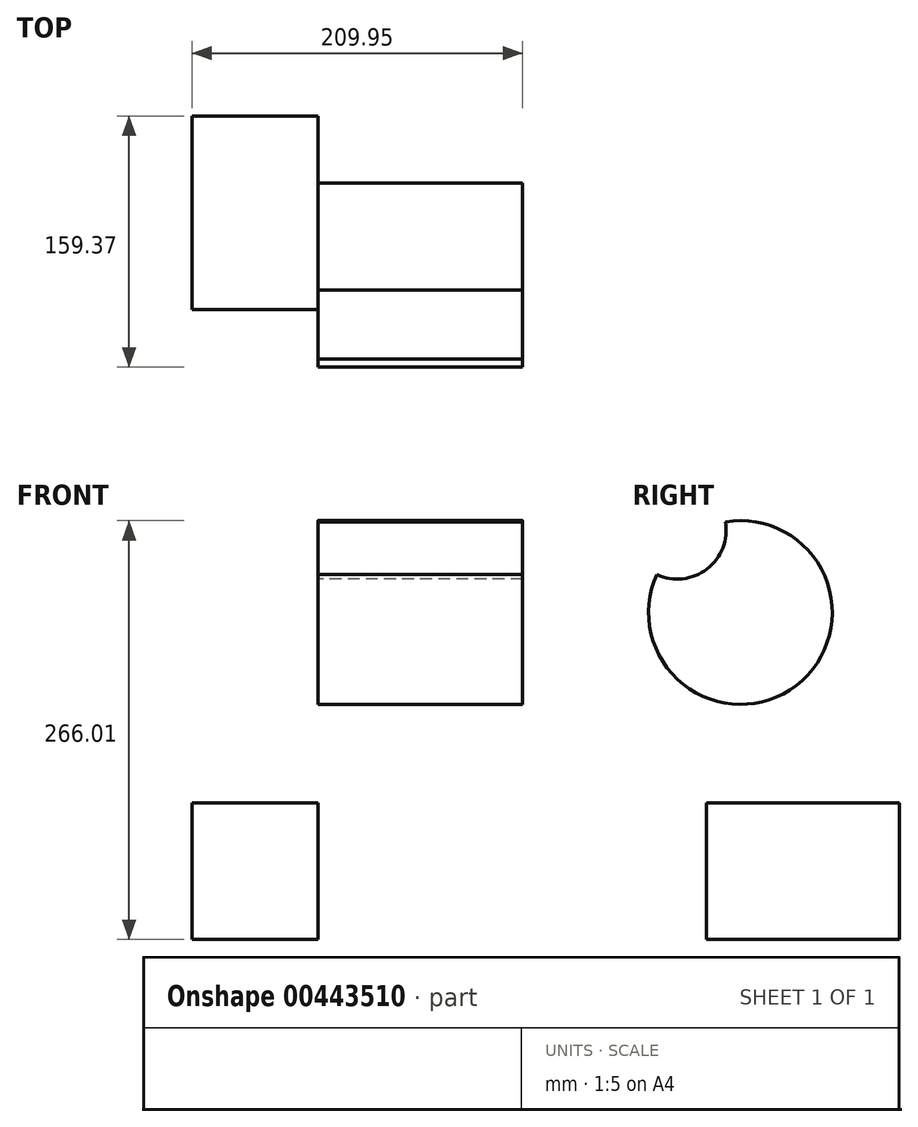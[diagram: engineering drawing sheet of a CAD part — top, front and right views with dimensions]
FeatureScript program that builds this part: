
annotation { "Feature Type Name" : "Feature", "Feature Type Description" : "" }
export const myFeature = defineFeature(function(context is Context, id is Id, definition is map)
    precondition{}
    {
        {
            var Q0;
            Q0=qCreatedBy(makeId("Right.planeOp"),FACE);
            var sketch = newSketch(context, id + "F0", { "sketchPlane" : qUnion([Q0])});
            skLineSegment(sketch, "E0.bottom", {"start": v(0, 0) * mm, "end": v(-122.72, 0) * mm});
            skLineSegment(sketch, "E0.top", {"start": v(0, -86.64) * mm, "end": v(-122.72, -86.64) * mm});
            skLineSegment(sketch, "E0.left", {"start": v(0, 0) * mm, "end": v(0, -86.64) * mm});
            skLineSegment(sketch, "E0.right", {"start": v(-122.72, 0) * mm, "end": v(-122.72, -86.64) * mm});
            skCircle(sketch, "E1", {"center": v(-101.02, 121.01) * mm, "radius": 58.36 * mm});
            skCircle(sketch, "E2", {"center": v(-141.05, 173.22) * mm, "radius": 31 * mm});
            skSolve(sketch);
        }
        {
            var Q0;
            Q0=makeQuery(id+"F0.imprint","IMPRINT",FACE,{"disambiguationData":[TD([[makeQuery(id+"F0.imprint","IMPRINT",EDGE,{"derivedFrom":sQuery(id+"F0.wireOp",EDGE,"E0.bottom")}),1.0]])]});
            extrude(context, id + "F1", {"entities" : qUnion([Q0]), "oppositeDirection" : true, "depth" : 79.9 * mm});
        }
        {
            var Q0;
            {var subQ0=sQuery(id+"F0.wireOp",EDGE,"E2");var subQ1=sQuery(id+"F0.wireOp",EDGE,"E1");var subQ2=makeQuery(id+"F0.imprint","INTERSECT",VERTEX,{"disambiguationData":[OD(0.0)],"derivedFrom":[subQ1,subQ0]});Q0=makeQuery(id+"F0.imprint","IMPRINT",FACE,{"disambiguationData":[TD([[makeQuery(id+"F0.imprint","IMPRINT",EDGE,{"disambiguationData":[TD([[subQ2,-1.0]])],"derivedFrom":subQ1}),1.0]])]});}
            extrude(context, id + "F2", {"entities" : qUnion([Q0]), "depth" : 130.05 * mm, "offsetDistance" : 25.4 * mm});
        }
    });
